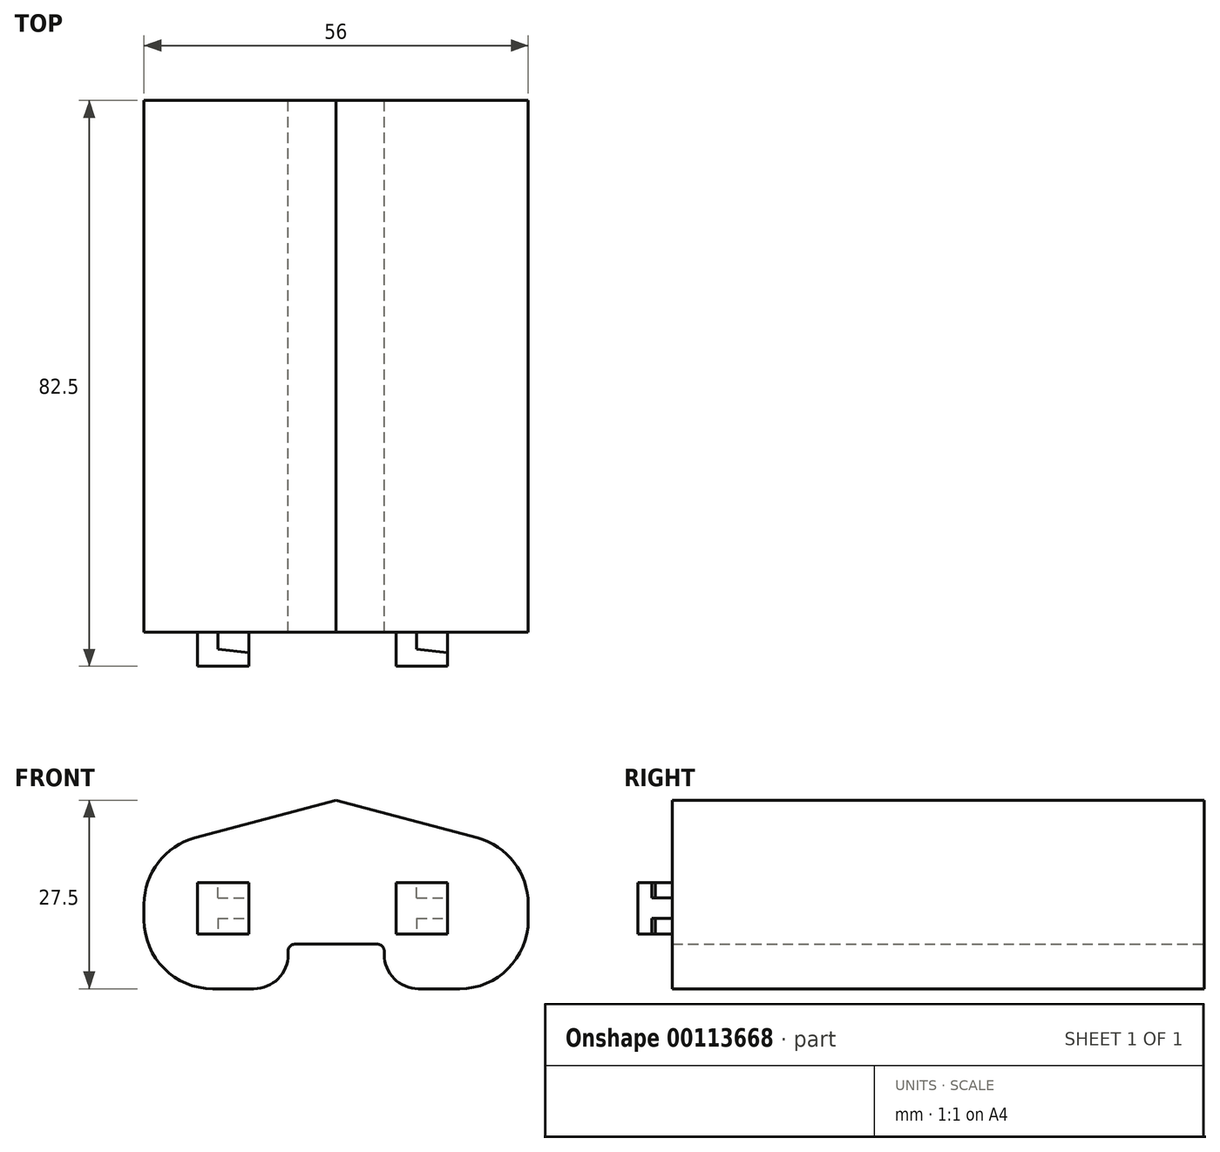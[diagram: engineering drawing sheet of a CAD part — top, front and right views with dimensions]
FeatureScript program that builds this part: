
annotation { "Feature Type Name" : "Feature", "Feature Type Description" : "" }
export const myFeature = defineFeature(function(context is Context, id is Id, definition is map)
    precondition{}
    {
        {
            var Q0;
            Q0=qCreatedBy(makeId("Front.planeOp"),FACE);
            var Q1;
            Q1=qCreatedBy(makeId("Front.planeOp"),FACE);
            var sketch = newSketch(context, id + "F0", { "sketchPlane" : qUnion([Q0, Q1])});
            skLineSegment(sketch, "E0", {"start": v(-18, -16.66) * mm, "end": v(-12, -16.66) * mm});
            skLineSegment(sketch, "E1", {"start": v(28, -6.66) * mm, "end": v(28, -4.33) * mm});
            skLineSegment(sketch, "E2", {"start": v(-28, -6.66) * mm, "end": v(-28, -4.33) * mm});
            skLineSegment(sketch, "E3", {"start": v(-20.59, 5.33) * mm, "end": v(0, 10.84) * mm});
            skLineSegment(sketch, "E4", {"start": v(0, 10.84) * mm, "end": v(20.59, 5.33) * mm});
            skPoint(sketch, "E5.visualSharp", {"position": v(-28, 3.34) * mm});
            skArc(sketch, "E5.filletArc", {"start": v(-20.59, 5.33) * mm, "mid": v(-25.93, 1.75) * mm, "end": v(-28, -4.33) * mm});
            skPoint(sketch, "E6.visualSharp", {"position": v(28, 3.34) * mm});
            skArc(sketch, "E6.filletArc", {"start": v(28, -4.33) * mm, "mid": v(25.93, 1.75) * mm, "end": v(20.59, 5.33) * mm});
            skPoint(sketch, "E7.visualSharp", {"position": v(-28, -16.66) * mm});
            skArc(sketch, "E7.filletArc", {"start": v(-28, -6.66) * mm, "mid": v(-25.07, -13.73) * mm, "end": v(-18, -16.66) * mm});
            skPoint(sketch, "E8.visualSharp", {"position": v(28, -16.66) * mm});
            skArc(sketch, "E8.filletArc", {"start": v(18, -16.66) * mm, "mid": v(25.07, -13.73) * mm, "end": v(28, -6.66) * mm});
            skLineSegment(sketch, "E9", {"start": v(-6, -10.16) * mm, "end": v(6, -10.16) * mm});
            skLineSegment(sketch, "E10", {"start": v(-7, -11.16) * mm, "end": v(-7, -11.66) * mm});
            skLineSegment(sketch, "E11", {"start": v(7, -11.16) * mm, "end": v(7, -11.66) * mm});
            skArc(sketch, "E12.filletArc", {"start": v(-12, -16.66) * mm, "mid": v(-8.46, -15.2) * mm, "end": v(-7, -11.66) * mm});
            skLineSegment(sketch, "E13", {"start": v(12, -16.66) * mm, "end": v(18, -16.66) * mm});
            skPoint(sketch, "E14.visualSharp", {"position": v(7, -16.66) * mm});
            skArc(sketch, "E14.filletArc", {"start": v(7, -11.66) * mm, "mid": v(8.46, -15.2) * mm, "end": v(12, -16.66) * mm});
            skPoint(sketch, "E15.visualSharp", {"position": v(-7, -10.16) * mm});
            skArc(sketch, "E15.filletArc", {"start": v(-6, -10.16) * mm, "mid": v(-6.7, -10.45) * mm, "end": v(-7, -11.16) * mm});
            skPoint(sketch, "E16.visualSharp", {"position": v(7, -10.16) * mm});
            skArc(sketch, "E16.filletArc", {"start": v(7, -11.16) * mm, "mid": v(6.7, -10.45) * mm, "end": v(6, -10.16) * mm});
            skSolve(sketch);
        }
        {
            var Q0;
            Q0 = qSketchRegion(id + "F0", true);
            extrude(context, id + "F1", {"entities" : qUnion([Q0]), "depth" : 77.5 * mm});
        }
        {
            var Q0;
            Q0=makeQuery(id+"F1.opExtrude","CAP_FACE",FACE,{"disambiguationData":[OSD([sQuery(id+"F0.wireOp",EDGE,"E0"),sQuery(id+"F0.wireOp",EDGE,"E1"),sQuery(id+"F0.wireOp",EDGE,"E2"),sQuery(id+"F0.wireOp",EDGE,"E3"),sQuery(id+"F0.wireOp",EDGE,"E4"),sQuery(id+"F0.wireOp",EDGE,"E5.filletArc"),sQuery(id+"F0.wireOp",EDGE,"E6.filletArc"),sQuery(id+"F0.wireOp",EDGE,"E7.filletArc"),sQuery(id+"F0.wireOp",EDGE,"E8.filletArc"),sQuery(id+"F0.wireOp",EDGE,"E9"),sQuery(id+"F0.wireOp",EDGE,"E10"),sQuery(id+"F0.wireOp",EDGE,"E11"),sQuery(id+"F0.wireOp",EDGE,"E12.filletArc"),sQuery(id+"F0.wireOp",EDGE,"E13"),sQuery(id+"F0.wireOp",EDGE,"E14.filletArc"),sQuery(id+"F0.wireOp",EDGE,"E15.filletArc"),sQuery(id+"F0.wireOp",EDGE,"E16.filletArc")])],"isStart":false});
            var sketch = newSketch(context, id + "F2", { "sketchPlane" : qUnion([Q0])});
            skLineSegment(sketch, "E17.bottom", {"start": v(-20.25, -1.16) * mm, "end": v(-12.75, -1.16) * mm});
            skLineSegment(sketch, "E17.top", {"start": v(-20.25, -8.66) * mm, "end": v(-12.75, -8.66) * mm});
            skLineSegment(sketch, "E17.left", {"start": v(-20.25, -1.16) * mm, "end": v(-20.25, -8.66) * mm});
            skLineSegment(sketch, "E17.right", {"start": v(-12.75, -1.16) * mm, "end": v(-12.75, -8.66) * mm});
            skLineSegment(sketch, "E18.bottom", {"start": v(8.75, -1.16) * mm, "end": v(16.25, -1.16) * mm});
            skLineSegment(sketch, "E18.top", {"start": v(8.75, -8.66) * mm, "end": v(16.25, -8.66) * mm});
            skLineSegment(sketch, "E18.left", {"start": v(8.75, -1.16) * mm, "end": v(8.75, -8.66) * mm});
            skLineSegment(sketch, "E18.right", {"start": v(16.25, -1.16) * mm, "end": v(16.25, -8.66) * mm});
            skSolve(sketch);
        }
        {
            var Q0;
            Q0 = qSketchRegion(id + "F2", true);
            extrude(context, id + "F3", {"entities" : qUnion([Q0]), "operationType" : NewBodyOperationType.ADD, "depth" : 5 * mm});
        }
        {
            var Q0;
            Q0=makeQuery(id+"F3.opExtrude","SWEPT_FACE",FACE,{"disambiguationData":[OSD([sQuery(id+"F2.wireOp",EDGE,"E17.bottom")])]});
            var sketch = newSketch(context, id + "F4", { "sketchPlane" : qUnion([Q0])});
            skLineSegment(sketch, "E19", {"start": v(-17.25, -77.5) * mm, "end": v(-17.25, -80) * mm});
            skLineSegment(sketch, "E20", {"start": v(-17.25, -80) * mm, "end": v(-12.75, -80.5) * mm});
            skLineSegment(sketch, "E21", {"start": v(-17.25, -77.5) * mm, "end": v(-12.75, -77.5) * mm});
            skLineSegment(sketch, "E22", {"start": v(-12.75, -77.5) * mm, "end": v(-12.75, -80.5) * mm});
            skSolve(sketch);
        }
        {
            var Q0;
            Q0=makeQuery(id+"F3.opExtrude","SWEPT_FACE",FACE,{"disambiguationData":[OSD([sQuery(id+"F2.wireOp",EDGE,"E18.bottom")])]});
            var sketch = newSketch(context, id + "F5", { "sketchPlane" : qUnion([Q0])});
            skLineSegment(sketch, "E23", {"start": v(11.75, -77.5) * mm, "end": v(11.75, -80) * mm});
            skLineSegment(sketch, "E24", {"start": v(11.75, -80) * mm, "end": v(16.25, -80.5) * mm});
            skLineSegment(sketch, "E25", {"start": v(11.75, -77.5) * mm, "end": v(16.25, -77.5) * mm});
            skLineSegment(sketch, "E26", {"start": v(16.25, -77.5) * mm, "end": v(16.25, -80.5) * mm});
            skSolve(sketch);
        }
        {
            var Q0;
            Q0 = qSketchRegion(id + "F4", true);
            extrude(context, id + "F6", {"entities" : qUnion([Q0]), "operationType" : NewBodyOperationType.REMOVE, "oppositeDirection" : true, "depth" : 2.25 * mm});
        }
        {
            var Q0;
            Q0 = qSketchRegion(id + "F5", true);
            extrude(context, id + "F7", {"entities" : qUnion([Q0]), "operationType" : NewBodyOperationType.REMOVE, "oppositeDirection" : true, "depth" : 2.25 * mm});
        }
        {
            var Q0;
            Q0=makeQuery(id+"F3.opExtrude","SWEPT_FACE",FACE,{"disambiguationData":[OSD([sQuery(id+"F2.wireOp",EDGE,"E18.top")])]});
            var sketch = newSketch(context, id + "F8", { "sketchPlane" : qUnion([Q0])});
            skLineSegment(sketch, "E27", {"start": v(11.75, 77.5) * mm, "end": v(11.75, 80) * mm});
            skLineSegment(sketch, "E28", {"start": v(11.75, 80) * mm, "end": v(16.25, 80.5) * mm});
            skLineSegment(sketch, "E29", {"start": v(16.25, 80.5) * mm, "end": v(16.25, 77.5) * mm});
            skLineSegment(sketch, "E30", {"start": v(16.25, 77.5) * mm, "end": v(11.75, 77.5) * mm});
            skSolve(sketch);
        }
        {
            var Q0;
            Q0=makeQuery(id+"F3.opExtrude","SWEPT_FACE",FACE,{"disambiguationData":[OSD([sQuery(id+"F2.wireOp",EDGE,"E17.top")])]});
            var sketch = newSketch(context, id + "F9", { "sketchPlane" : qUnion([Q0])});
            skLineSegment(sketch, "E31", {"start": v(-17.25, 77.5) * mm, "end": v(-17.25, 80) * mm});
            skLineSegment(sketch, "E32", {"start": v(-17.25, 80) * mm, "end": v(-12.75, 80.5) * mm});
            skLineSegment(sketch, "E33", {"start": v(-17.25, 77.5) * mm, "end": v(-12.75, 77.5) * mm});
            skLineSegment(sketch, "E34", {"start": v(-12.75, 77.5) * mm, "end": v(-12.75, 80.5) * mm});
            skSolve(sketch);
        }
        {
            var Q0;
            Q0 = qSketchRegion(id + "F8", true);
            extrude(context, id + "F10", {"entities" : qUnion([Q0]), "operationType" : NewBodyOperationType.REMOVE, "oppositeDirection" : true, "depth" : 2.25 * mm});
        }
        {
            var Q0;
            Q0 = qSketchRegion(id + "F9", true);
            extrude(context, id + "F11", {"entities" : qUnion([Q0]), "operationType" : NewBodyOperationType.REMOVE, "oppositeDirection" : true, "depth" : 2.25 * mm});
        }
    });
